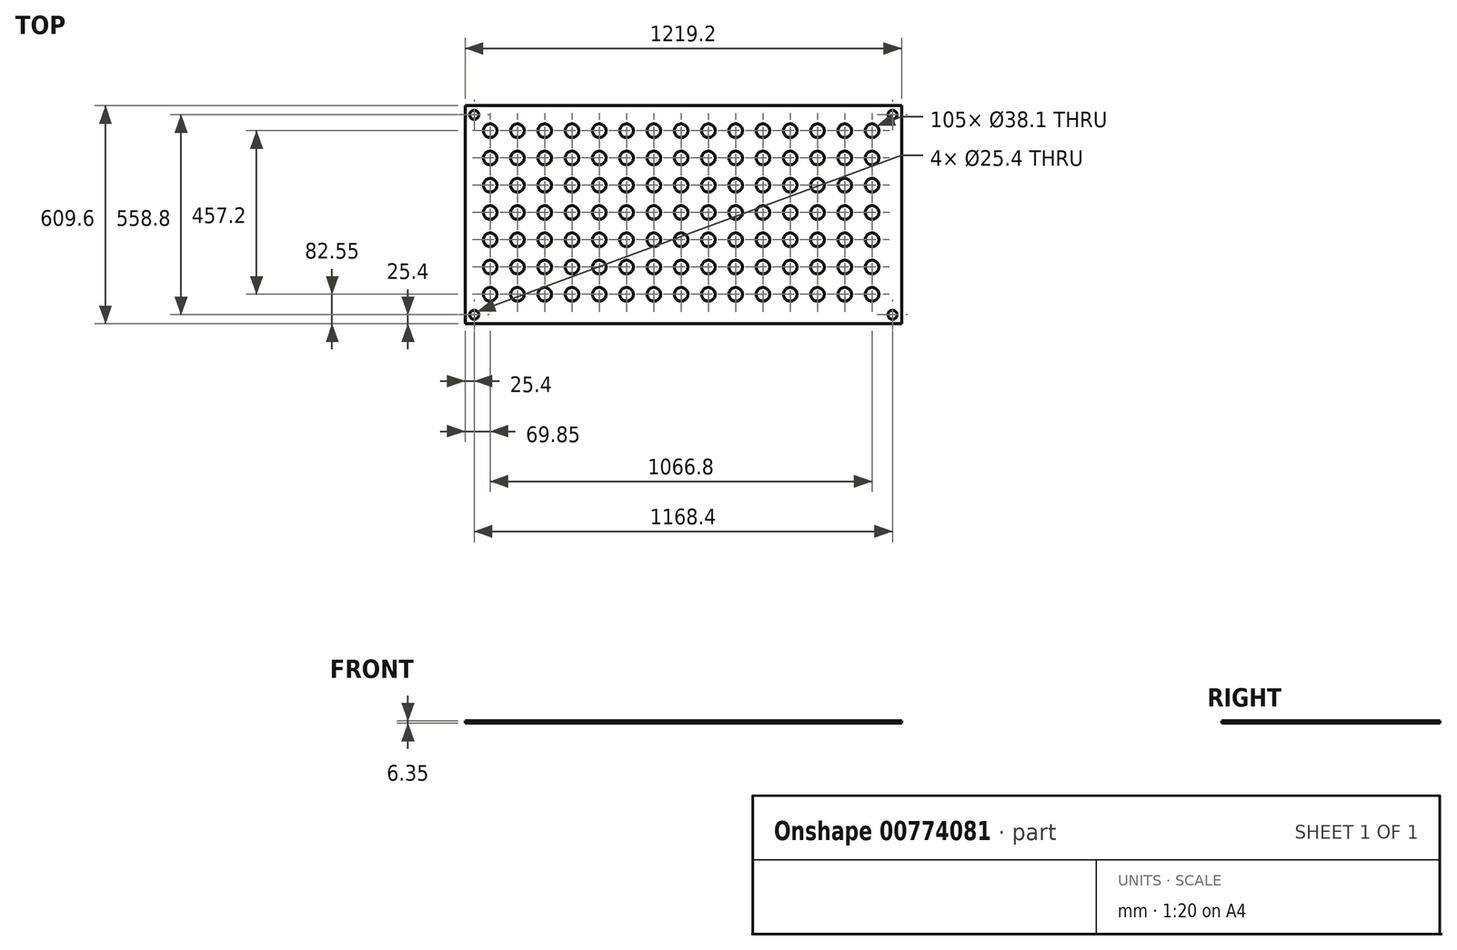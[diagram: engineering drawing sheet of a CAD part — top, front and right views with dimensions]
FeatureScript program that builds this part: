
annotation { "Feature Type Name" : "Feature", "Feature Type Description" : "" }
export const myFeature = defineFeature(function(context is Context, id is Id, definition is map)
    precondition{}
    {
        {
            var Q0;
            Q0=qCreatedBy(makeId("Top.planeOp"),FACE);
            var sketch = newSketch(context, id + "F0", { "sketchPlane" : qUnion([Q0])});
            skLineSegment(sketch, "E0.bottom", {"start": v(0, 0) * mm, "end": v(1219.2, 0) * mm});
            skLineSegment(sketch, "E0.top", {"start": v(0, 609.6) * mm, "end": v(1219.2, 609.6) * mm});
            skLineSegment(sketch, "E0.left", {"start": v(0, 0) * mm, "end": v(0, 609.6) * mm});
            skLineSegment(sketch, "E0.right", {"start": v(1219.2, 0) * mm, "end": v(1219.2, 609.6) * mm});
            skSolve(sketch);
        }
        {
            var Q0;
            Q0=makeQuery(id+"F0.imprint","IMPRINT",FACE,{"disambiguationData":[TD([[makeQuery(id+"F0.imprint","IMPRINT",EDGE,{"derivedFrom":sQuery(id+"F0.wireOp",EDGE,"E0.bottom")}),1.0]])]});
            extrude(context, id + "F1", {"entities" : qUnion([Q0]), "depth" : 6.35 * mm, "offsetDistance" : 25.4 * mm});
        }
        {
            var Q0;
            Q0=makeQuery(id+"F1.opExtrude","CAP_FACE",FACE,{"disambiguationData":[OSD([sQuery(id+"F0.wireOp",EDGE,"E0.bottom"),sQuery(id+"F0.wireOp",EDGE,"E0.top"),sQuery(id+"F0.wireOp",EDGE,"E0.left"),sQuery(id+"F0.wireOp",EDGE,"E0.right")])],"isStart":false});
            var sketch = newSketch(context, id + "F2", { "sketchPlane" : qUnion([Q0])});
            skCircle(sketch, "E1", {"center": v(69.85, 539.75) * mm, "radius": 19.05 * mm});
            skCircle(sketch, "E2.1.0.0", {"center": v(146.05, 539.75) * mm, "radius": 19.05 * mm});
            skCircle(sketch, "E2.2.0.0", {"center": v(222.25, 539.75) * mm, "radius": 19.05 * mm});
            skLineSegment(sketch, "E2.direction1", {"start": v(69.85, 539.75) * mm, "end": v(146.05, 539.75) * mm, "construction": true});
            skCircle(sketch, "E3.0.3.0", {"center": v(298.45, 539.75) * mm, "radius": 19.05 * mm});
            skCircle(sketch, "E3.0.4.0", {"center": v(374.65, 539.75) * mm, "radius": 19.05 * mm});
            skCircle(sketch, "E3.0.5.0", {"center": v(450.85, 539.75) * mm, "radius": 19.05 * mm});
            skCircle(sketch, "E3.0.6.0", {"center": v(527.05, 539.75) * mm, "radius": 19.05 * mm});
            skCircle(sketch, "E3.0.7.0", {"center": v(603.25, 539.75) * mm, "radius": 19.05 * mm});
            skCircle(sketch, "E3.0.8.0", {"center": v(679.45, 539.75) * mm, "radius": 19.05 * mm});
            skCircle(sketch, "E3.0.9.0", {"center": v(755.65, 539.75) * mm, "radius": 19.05 * mm});
            skCircle(sketch, "E4.0.10.0", {"center": v(831.85, 539.75) * mm, "radius": 19.05 * mm});
            skCircle(sketch, "E4.0.11.0", {"center": v(908.05, 539.75) * mm, "radius": 19.05 * mm});
            skCircle(sketch, "E4.0.12.0", {"center": v(984.25, 539.75) * mm, "radius": 19.05 * mm});
            skCircle(sketch, "E4.0.13.0", {"center": v(1060.45, 539.75) * mm, "radius": 19.05 * mm});
            skCircle(sketch, "E4.0.14.0", {"center": v(1136.65, 539.75) * mm, "radius": 19.05 * mm});
            skCircle(sketch, "E5.0.1.0", {"center": v(69.85, 463.55) * mm, "radius": 19.05 * mm});
            skCircle(sketch, "E5.0.1.1", {"center": v(222.25, 463.55) * mm, "radius": 19.05 * mm});
            skCircle(sketch, "E5.0.1.2", {"center": v(146.05, 463.55) * mm, "radius": 19.05 * mm});
            skCircle(sketch, "E5.0.1.3", {"center": v(298.45, 463.55) * mm, "radius": 19.05 * mm});
            skCircle(sketch, "E5.0.1.4", {"center": v(374.65, 463.55) * mm, "radius": 19.05 * mm});
            skCircle(sketch, "E5.0.1.5", {"center": v(450.85, 463.55) * mm, "radius": 19.05 * mm});
            skCircle(sketch, "E5.0.1.6", {"center": v(527.05, 463.55) * mm, "radius": 19.05 * mm});
            skCircle(sketch, "E5.0.1.7", {"center": v(603.25, 463.55) * mm, "radius": 19.05 * mm});
            skCircle(sketch, "E5.0.1.8", {"center": v(679.45, 463.55) * mm, "radius": 19.05 * mm});
            skCircle(sketch, "E5.0.1.9", {"center": v(755.65, 463.55) * mm, "radius": 19.05 * mm});
            skCircle(sketch, "E5.0.1.10", {"center": v(831.85, 463.55) * mm, "radius": 19.05 * mm});
            skCircle(sketch, "E5.0.1.11", {"center": v(908.05, 463.55) * mm, "radius": 19.05 * mm});
            skCircle(sketch, "E5.0.1.12", {"center": v(984.25, 463.55) * mm, "radius": 19.05 * mm});
            skCircle(sketch, "E5.0.1.13", {"center": v(1060.45, 463.55) * mm, "radius": 19.05 * mm});
            skCircle(sketch, "E5.0.1.14", {"center": v(1136.65, 463.55) * mm, "radius": 19.05 * mm});
            skCircle(sketch, "E5.0.2.0", {"center": v(69.85, 387.35) * mm, "radius": 19.05 * mm});
            skCircle(sketch, "E5.0.2.1", {"center": v(222.25, 387.35) * mm, "radius": 19.05 * mm});
            skCircle(sketch, "E5.0.2.2", {"center": v(146.05, 387.35) * mm, "radius": 19.05 * mm});
            skCircle(sketch, "E5.0.2.3", {"center": v(298.45, 387.35) * mm, "radius": 19.05 * mm});
            skCircle(sketch, "E5.0.2.4", {"center": v(374.65, 387.35) * mm, "radius": 19.05 * mm});
            skCircle(sketch, "E5.0.2.5", {"center": v(450.85, 387.35) * mm, "radius": 19.05 * mm});
            skCircle(sketch, "E5.0.2.6", {"center": v(527.05, 387.35) * mm, "radius": 19.05 * mm});
            skCircle(sketch, "E5.0.2.7", {"center": v(603.25, 387.35) * mm, "radius": 19.05 * mm});
            skCircle(sketch, "E5.0.2.8", {"center": v(679.45, 387.35) * mm, "radius": 19.05 * mm});
            skCircle(sketch, "E5.0.2.9", {"center": v(755.65, 387.35) * mm, "radius": 19.05 * mm});
            skCircle(sketch, "E5.0.2.10", {"center": v(831.85, 387.35) * mm, "radius": 19.05 * mm});
            skCircle(sketch, "E5.0.2.11", {"center": v(908.05, 387.35) * mm, "radius": 19.05 * mm});
            skCircle(sketch, "E5.0.2.12", {"center": v(984.25, 387.35) * mm, "radius": 19.05 * mm});
            skCircle(sketch, "E5.0.2.13", {"center": v(1060.45, 387.35) * mm, "radius": 19.05 * mm});
            skCircle(sketch, "E5.0.2.14", {"center": v(1136.65, 387.35) * mm, "radius": 19.05 * mm});
            skCircle(sketch, "E5.0.3.0", {"center": v(69.85, 311.15) * mm, "radius": 19.05 * mm});
            skCircle(sketch, "E5.0.3.1", {"center": v(222.25, 311.15) * mm, "radius": 19.05 * mm});
            skCircle(sketch, "E5.0.3.2", {"center": v(146.05, 311.15) * mm, "radius": 19.05 * mm});
            skCircle(sketch, "E5.0.3.3", {"center": v(298.45, 311.15) * mm, "radius": 19.05 * mm});
            skCircle(sketch, "E5.0.3.4", {"center": v(374.65, 311.15) * mm, "radius": 19.05 * mm});
            skCircle(sketch, "E5.0.3.5", {"center": v(450.85, 311.15) * mm, "radius": 19.05 * mm});
            skCircle(sketch, "E5.0.3.6", {"center": v(527.05, 311.15) * mm, "radius": 19.05 * mm});
            skCircle(sketch, "E5.0.3.7", {"center": v(603.25, 311.15) * mm, "radius": 19.05 * mm});
            skCircle(sketch, "E5.0.3.8", {"center": v(679.45, 311.15) * mm, "radius": 19.05 * mm});
            skCircle(sketch, "E5.0.3.9", {"center": v(755.65, 311.15) * mm, "radius": 19.05 * mm});
            skCircle(sketch, "E5.0.3.10", {"center": v(831.85, 311.15) * mm, "radius": 19.05 * mm});
            skCircle(sketch, "E5.0.3.11", {"center": v(908.05, 311.15) * mm, "radius": 19.05 * mm});
            skCircle(sketch, "E5.0.3.12", {"center": v(984.25, 311.15) * mm, "radius": 19.05 * mm});
            skCircle(sketch, "E5.0.3.13", {"center": v(1060.45, 311.15) * mm, "radius": 19.05 * mm});
            skCircle(sketch, "E5.0.3.14", {"center": v(1136.65, 311.15) * mm, "radius": 19.05 * mm});
            skCircle(sketch, "E5.0.4.0", {"center": v(69.85, 234.95) * mm, "radius": 19.05 * mm});
            skCircle(sketch, "E5.0.4.1", {"center": v(222.25, 234.95) * mm, "radius": 19.05 * mm});
            skCircle(sketch, "E5.0.4.2", {"center": v(146.05, 234.95) * mm, "radius": 19.05 * mm});
            skCircle(sketch, "E5.0.4.3", {"center": v(298.45, 234.95) * mm, "radius": 19.05 * mm});
            skCircle(sketch, "E5.0.4.4", {"center": v(374.65, 234.95) * mm, "radius": 19.05 * mm});
            skCircle(sketch, "E5.0.4.5", {"center": v(450.85, 234.95) * mm, "radius": 19.05 * mm});
            skCircle(sketch, "E5.0.4.6", {"center": v(527.05, 234.95) * mm, "radius": 19.05 * mm});
            skCircle(sketch, "E5.0.4.7", {"center": v(603.25, 234.95) * mm, "radius": 19.05 * mm});
            skCircle(sketch, "E5.0.4.8", {"center": v(679.45, 234.95) * mm, "radius": 19.05 * mm});
            skCircle(sketch, "E5.0.4.9", {"center": v(755.65, 234.95) * mm, "radius": 19.05 * mm});
            skCircle(sketch, "E5.0.4.10", {"center": v(831.85, 234.95) * mm, "radius": 19.05 * mm});
            skCircle(sketch, "E5.0.4.11", {"center": v(908.05, 234.95) * mm, "radius": 19.05 * mm});
            skCircle(sketch, "E5.0.4.12", {"center": v(984.25, 234.95) * mm, "radius": 19.05 * mm});
            skCircle(sketch, "E5.0.4.13", {"center": v(1060.45, 234.95) * mm, "radius": 19.05 * mm});
            skCircle(sketch, "E5.0.4.14", {"center": v(1136.65, 234.95) * mm, "radius": 19.05 * mm});
            skCircle(sketch, "E5.0.5.0", {"center": v(69.85, 158.75) * mm, "radius": 19.05 * mm});
            skCircle(sketch, "E5.0.5.1", {"center": v(222.25, 158.75) * mm, "radius": 19.05 * mm});
            skCircle(sketch, "E5.0.5.2", {"center": v(146.05, 158.75) * mm, "radius": 19.05 * mm});
            skCircle(sketch, "E5.0.5.3", {"center": v(298.45, 158.75) * mm, "radius": 19.05 * mm});
            skCircle(sketch, "E5.0.5.4", {"center": v(374.65, 158.75) * mm, "radius": 19.05 * mm});
            skCircle(sketch, "E5.0.5.5", {"center": v(450.85, 158.75) * mm, "radius": 19.05 * mm});
            skCircle(sketch, "E5.0.5.6", {"center": v(527.05, 158.75) * mm, "radius": 19.05 * mm});
            skCircle(sketch, "E5.0.5.7", {"center": v(603.25, 158.75) * mm, "radius": 19.05 * mm});
            skCircle(sketch, "E5.0.5.8", {"center": v(679.45, 158.75) * mm, "radius": 19.05 * mm});
            skCircle(sketch, "E5.0.5.9", {"center": v(755.65, 158.75) * mm, "radius": 19.05 * mm});
            skCircle(sketch, "E5.0.5.10", {"center": v(831.85, 158.75) * mm, "radius": 19.05 * mm});
            skCircle(sketch, "E5.0.5.11", {"center": v(908.05, 158.75) * mm, "radius": 19.05 * mm});
            skCircle(sketch, "E5.0.5.12", {"center": v(984.25, 158.75) * mm, "radius": 19.05 * mm});
            skCircle(sketch, "E5.0.5.13", {"center": v(1060.45, 158.75) * mm, "radius": 19.05 * mm});
            skCircle(sketch, "E5.0.5.14", {"center": v(1136.65, 158.75) * mm, "radius": 19.05 * mm});
            skCircle(sketch, "E5.0.6.0", {"center": v(69.85, 82.55) * mm, "radius": 19.05 * mm});
            skCircle(sketch, "E5.0.6.1", {"center": v(222.25, 82.55) * mm, "radius": 19.05 * mm});
            skCircle(sketch, "E5.0.6.2", {"center": v(146.05, 82.55) * mm, "radius": 19.05 * mm});
            skCircle(sketch, "E5.0.6.3", {"center": v(298.45, 82.55) * mm, "radius": 19.05 * mm});
            skCircle(sketch, "E5.0.6.4", {"center": v(374.65, 82.55) * mm, "radius": 19.05 * mm});
            skCircle(sketch, "E5.0.6.5", {"center": v(450.85, 82.55) * mm, "radius": 19.05 * mm});
            skCircle(sketch, "E5.0.6.6", {"center": v(527.05, 82.55) * mm, "radius": 19.05 * mm});
            skCircle(sketch, "E5.0.6.7", {"center": v(603.25, 82.55) * mm, "radius": 19.05 * mm});
            skCircle(sketch, "E5.0.6.8", {"center": v(679.45, 82.55) * mm, "radius": 19.05 * mm});
            skCircle(sketch, "E5.0.6.9", {"center": v(755.65, 82.55) * mm, "radius": 19.05 * mm});
            skCircle(sketch, "E5.0.6.10", {"center": v(831.85, 82.55) * mm, "radius": 19.05 * mm});
            skCircle(sketch, "E5.0.6.11", {"center": v(908.05, 82.55) * mm, "radius": 19.05 * mm});
            skCircle(sketch, "E5.0.6.12", {"center": v(984.25, 82.55) * mm, "radius": 19.05 * mm});
            skCircle(sketch, "E5.0.6.13", {"center": v(1060.45, 82.55) * mm, "radius": 19.05 * mm});
            skCircle(sketch, "E5.0.6.14", {"center": v(1136.65, 82.55) * mm, "radius": 19.05 * mm});
            skLineSegment(sketch, "E5.direction1", {"start": v(69.85, 539.75) * mm, "end": v(95.25, 539.75) * mm, "construction": true});
            skLineSegment(sketch, "E5.direction2", {"start": v(69.85, 539.75) * mm, "end": v(69.85, 463.55) * mm, "construction": true});
            skSolve(sketch);
        }
        {
            var Q0;
            Q0 = qSketchRegion(id + "F2", true);
            extrude(context, id + "F3", {"entities" : qUnion([Q0]), "operationType" : NewBodyOperationType.REMOVE, "endBound" : BoundingType.UP_TO_NEXT, "oppositeDirection" : true, "depth" : 25.4 * mm, "offsetDistance" : 25.4 * mm});
        }
        {
            var Q0;
            Q0=makeQuery(id+"F1.opExtrude","CAP_FACE",FACE,{"disambiguationData":[OSD([sQuery(id+"F0.wireOp",EDGE,"E0.bottom"),sQuery(id+"F0.wireOp",EDGE,"E0.top"),sQuery(id+"F0.wireOp",EDGE,"E0.left"),sQuery(id+"F0.wireOp",EDGE,"E0.right")])],"isStart":false});
            var sketch = newSketch(context, id + "F4", { "sketchPlane" : qUnion([Q0])});
            skCircle(sketch, "E6", {"center": v(25.4, 584.2) * mm, "radius": 12.7 * mm});
            skCircle(sketch, "E7", {"center": v(25.4, 25.4) * mm, "radius": 12.7 * mm});
            skCircle(sketch, "E8", {"center": v(1193.8, 25.4) * mm, "radius": 12.7 * mm});
            skCircle(sketch, "E9", {"center": v(1193.8, 584.2) * mm, "radius": 12.7 * mm});
            skSolve(sketch);
        }
        {
            var Q0;
            Q0 = qSketchRegion(id + "F4", true);
            extrude(context, id + "F5", {"entities" : qUnion([Q0]), "operationType" : NewBodyOperationType.REMOVE, "endBound" : BoundingType.UP_TO_NEXT, "oppositeDirection" : true, "depth" : 25.4 * mm, "offsetDistance" : 25.4 * mm});
        }
    });
